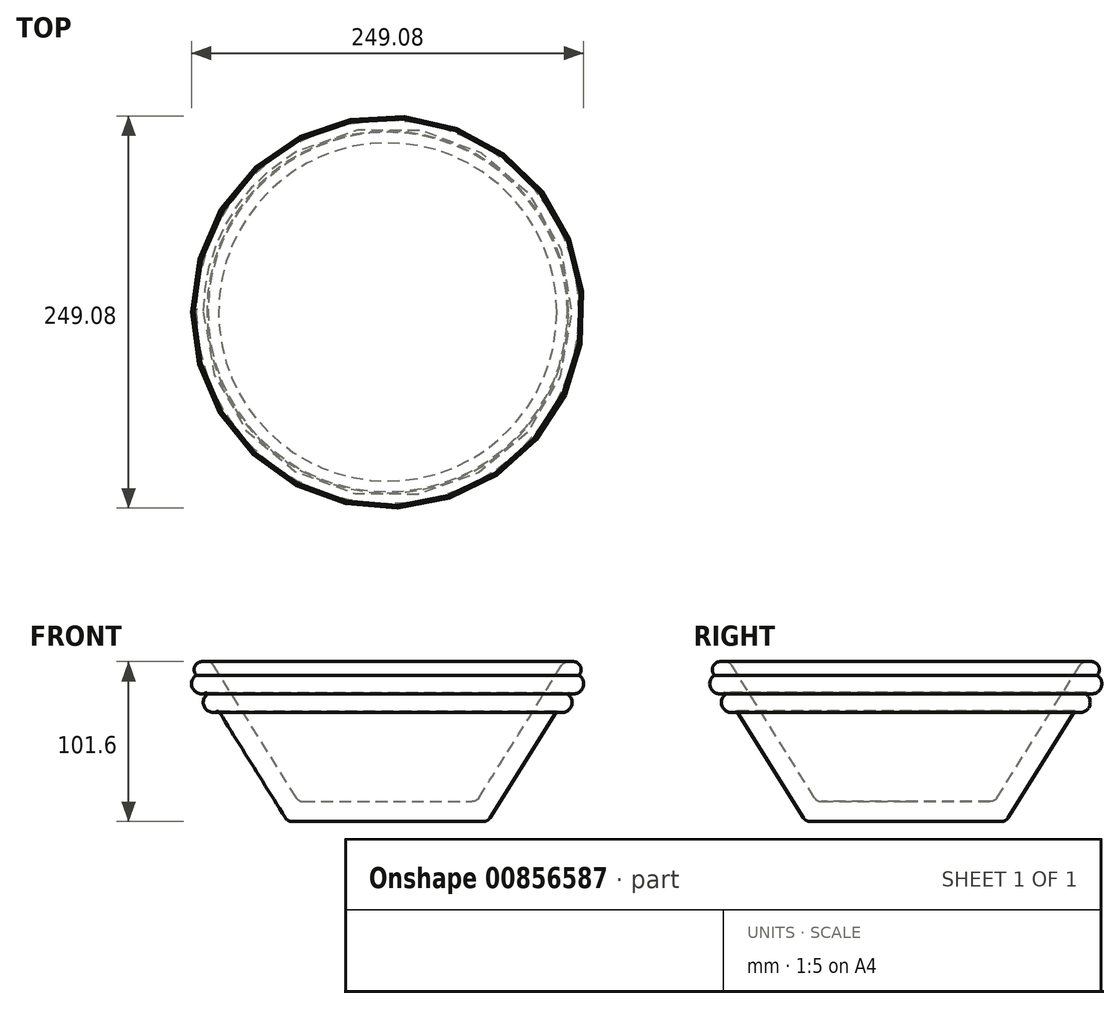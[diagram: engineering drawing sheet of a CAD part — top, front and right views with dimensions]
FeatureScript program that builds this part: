
annotation { "Feature Type Name" : "Feature", "Feature Type Description" : "" }
export const myFeature = defineFeature(function(context is Context, id is Id, definition is map)
    precondition{}
    {
        {
            var Q0;
            Q0=qCreatedBy(makeId("Front.planeOp"),FACE);
            var sketch = newSketch(context, id + "F0", { "sketchPlane" : qUnion([Q0])});
            skLineSegment(sketch, "E0", {"start": v(0, 0) * mm, "end": v(0, 101.6) * mm, "construction": true});
            skLineSegment(sketch, "E1", {"start": v(0, 0) * mm, "end": v(63.5, 0) * mm});
            skLineSegment(sketch, "E2", {"start": v(63.5, 0) * mm, "end": v(127, 101.6) * mm});
            skLineSegment(sketch, "E3.0", {"start": v(56.46, 12.7) * mm, "end": v(112.02, 101.6) * mm});
            skLineSegment(sketch, "E3.1", {"start": v(0, 12.7) * mm, "end": v(56.46, 12.7) * mm});
            skLineSegment(sketch, "E4", {"start": v(112.02, 101.6) * mm, "end": v(127, 101.6) * mm});
            skLineSegment(sketch, "E5", {"start": v(0, 12.7) * mm, "end": v(0, 0) * mm});
            skArc(sketch, "E6", {"start": v(114.83, 82.12) * mm, "mid": v(123.58, 84.14) * mm, "end": v(121.56, 92.89) * mm});
            skArc(sketch, "E7", {"start": v(107.42, 70.27) * mm, "mid": v(116.17, 72.3) * mm, "end": v(114.15, 81.04) * mm});
            skSolve(sketch);
        }
        {
            var Q0;
            Q0=makeQuery(id+"F0.imprint","IMPRINT",FACE,{"disambiguationData":[TD([[makeQuery(id+"F0.imprint","IMPRINT",EDGE,{"derivedFrom":sQuery(id+"F0.wireOp",EDGE,"E1")}),1.0]])]});
            var Q1;
            {var subQ0=sQuery(id+"F0.wireOp",EDGE,"E6");Q1=makeQuery(id+"F0.imprint","IMPRINT",FACE,{"disambiguationData":[TD([[makeQuery(id+"F0.imprint","IMPRINT",EDGE,{"derivedFrom":subQ0}),1.0]])]});}
            var Q2;
            {var subQ0=sQuery(id+"F0.wireOp",EDGE,"E7");Q2=makeQuery(id+"F0.imprint","IMPRINT",FACE,{"disambiguationData":[TD([[makeQuery(id+"F0.imprint","IMPRINT",EDGE,{"derivedFrom":subQ0}),1.0]])]});}
            var Q3;
            Q3=sQuery(id+"F0.wireOp",EDGE,"E0");
            revolve(context, id + "F1", {"surfaceOperationType" : NewSurfaceOperationType.NEW, "entities" : qUnion([Q0, Q1, Q2]), "axis" : qUnion([Q3]), "revolveType" : RevolveType.FULL});
        }
        {
            var Q0;
            Q0=makeQuery(id+"F1.opRevolve","SWEPT_EDGE",EDGE,{"disambiguationData":[OSD([sQuery(id+"F0.wireOp",EDGE,"E3.0"),sQuery(id+"F0.wireOp",EDGE,"E3.1")])]});
            var Q1;
            Q1=makeQuery(id+"F1.opRevolve","SWEPT_EDGE",EDGE,{"disambiguationData":[OSD([sQuery(id+"F0.wireOp",EDGE,"E3.0"),sQuery(id+"F0.wireOp",EDGE,"E4")])]});
            var Q2;
            Q2=makeQuery(id+"F1.opRevolve","SWEPT_EDGE",EDGE,{"disambiguationData":[OSD([sQuery(id+"F0.wireOp",EDGE,"E2"),sQuery(id+"F0.wireOp",EDGE,"E4")])]});
            var Q3;
            Q3=makeQuery(id+"F1.opRevolve","SWEPT_EDGE",EDGE,{"disambiguationData":[OSD([sQuery(id+"F0.wireOp",EDGE,"E1"),sQuery(id+"F0.wireOp",EDGE,"E2")])]});
            fillet(context, id + "F2", {"entities" : qUnion([Q0, Q1, Q2, Q3]), "radius" : 5.08 * mm, "tangentPropagation" : true, "allowEdgeOverflow" : false});
        }
    });
